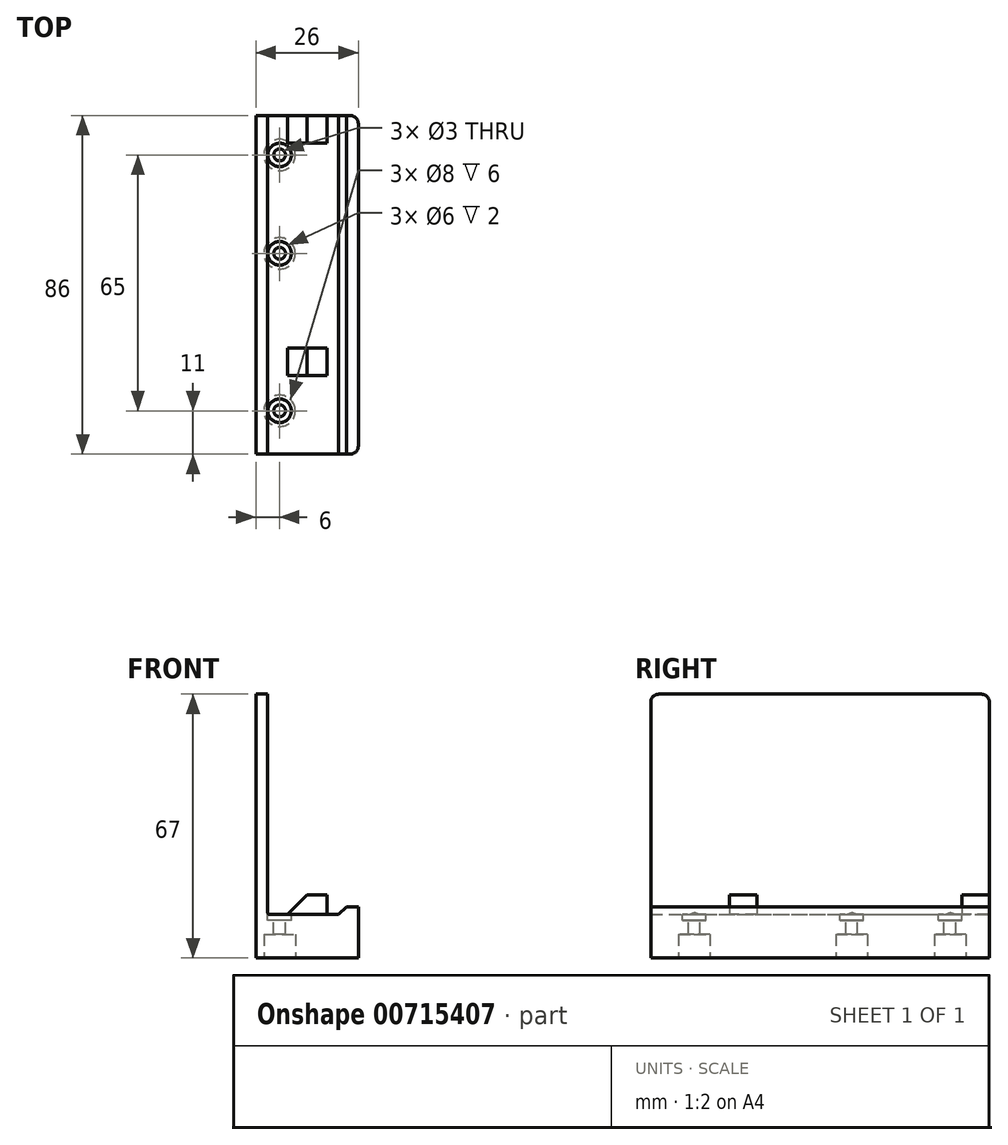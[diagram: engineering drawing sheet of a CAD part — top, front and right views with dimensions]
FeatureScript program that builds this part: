
annotation { "Feature Type Name" : "Feature", "Feature Type Description" : "" }
export const myFeature = defineFeature(function(context is Context, id is Id, definition is map)
    precondition{}
    {
        {
            var Q0;
            Q0=qCreatedBy(makeId("Front.planeOp"),FACE);
            var sketch = newSketch(context, id + "F0", { "sketchPlane" : qUnion([Q0])});
            skLineSegment(sketch, "E0", {"start": v(0, 67) * mm, "end": v(0, 11.5) * mm});
            skLineSegment(sketch, "E1", {"start": v(0, 67) * mm, "end": v(-3, 67) * mm});
            skLineSegment(sketch, "E2", {"start": v(-3, 67) * mm, "end": v(-3, 0) * mm});
            skLineSegment(sketch, "E3", {"start": v(-3, 0) * mm, "end": v(23, 0) * mm});
            skLineSegment(sketch, "E4", {"start": v(0.5, 11) * mm, "end": v(18, 11) * mm});
            skPoint(sketch, "E5.visualSharp", {"position": v(0, 11) * mm});
            skArc(sketch, "E5.filletArc", {"start": v(0, 11.5) * mm, "mid": v(0.15, 11.15) * mm, "end": v(0.5, 11) * mm});
            skLineSegment(sketch, "E6", {"start": v(20, 13) * mm, "end": v(23, 13) * mm});
            skLineSegment(sketch, "E7", {"start": v(23, 13) * mm, "end": v(23, 0) * mm});
            skLineSegment(sketch, "E8", {"start": v(18, 11) * mm, "end": v(20, 13) * mm});
            skSolve(sketch);
        }
        {
            var Q0;
            Q0=qSketchRegion(id+"F0",true);
            extrude(context, id + "F1", {"entities" : qUnion([Q0]), "endBound" : BoundingType.SYMMETRIC, "depth" : 86 * mm});
        }
        {
            var Q0;
            Q0=makeQuery(id+"F1.opExtrude","SWEPT_FACE",FACE,{"disambiguationData":[OSD([sQuery(id+"F0.wireOp",EDGE,"E3")])]});
            var sketch = newSketch(context, id + "F2", { "sketchPlane" : qUnion([Q0])});
            skCircle(sketch, "E9", {"center": v(3, -33) * mm, "radius": 4 * mm});
            skCircle(sketch, "E10", {"center": v(3, -8) * mm, "radius": 4 * mm});
            skCircle(sketch, "E11", {"center": v(3, 32) * mm, "radius": 4 * mm});
            skLineSegment(sketch, "E12", {"start": v(3, -46.09) * mm, "end": v(3, 49.3) * mm, "construction": true});
            skLineSegment(sketch, "E13", {"start": v(-6.86, -33) * mm, "end": v(12.39, -33) * mm, "construction": true});
            skLineSegment(sketch, "E14", {"start": v(-7.6, -8) * mm, "end": v(13.66, -8) * mm, "construction": true});
            skLineSegment(sketch, "E15", {"start": v(-7.39, 32) * mm, "end": v(13.66, 32) * mm, "construction": true});
            skSolve(sketch);
        }
        {
            var Q0;
            Q0=qSketchRegion(id+"F2",true);
            extrude(context, id + "F3", {"entities" : qUnion([Q0]), "operationType" : NewBodyOperationType.REMOVE, "oppositeDirection" : true, "depth" : 6 * mm});
        }
        {
            var Q0;
            Q0=makeQuery(id+"F1.opExtrude","SWEPT_FACE",FACE,{"disambiguationData":[OSD([sQuery(id+"F0.wireOp",EDGE,"E4")])]});
            var sketch = newSketch(context, id + "F4", { "sketchPlane" : qUnion([Q0])});
            skCircle(sketch, "E16", {"center": v(3, 33) * mm, "radius": 1.5 * mm});
            skCircle(sketch, "E17", {"center": v(3, 8) * mm, "radius": 1.5 * mm});
            skCircle(sketch, "E18", {"center": v(3, -32) * mm, "radius": 1.5 * mm});
            skCircle(sketch, "E19", {"center": v(3, 8) * mm, "radius": 3 * mm});
            skCircle(sketch, "E20", {"center": v(3, 33) * mm, "radius": 3 * mm});
            skCircle(sketch, "E21", {"center": v(3, -32) * mm, "radius": 3 * mm});
            skSolve(sketch);
        }
        {
            var Q0;
            Q0=makeQuery(id+"F4.imprint","IMPRINT",FACE,{"disambiguationData":[TD([[makeQuery(id+"F4.imprint","IMPRINT",EDGE,{"derivedFrom":sQuery(id+"F4.wireOp",EDGE,"E16")}),1.0]])]});
            var Q1;
            Q1=makeQuery(id+"F4.imprint","IMPRINT",FACE,{"disambiguationData":[TD([[makeQuery(id+"F4.imprint","IMPRINT",EDGE,{"derivedFrom":sQuery(id+"F4.wireOp",EDGE,"E17")}),1.0]])]});
            var Q2;
            Q2=makeQuery(id+"F4.imprint","IMPRINT",FACE,{"disambiguationData":[TD([[makeQuery(id+"F4.imprint","IMPRINT",EDGE,{"derivedFrom":sQuery(id+"F4.wireOp",EDGE,"E18")}),1.0]])]});
            extrude(context, id + "F5", {"entities" : qUnion([Q0, Q1, Q2]), "operationType" : NewBodyOperationType.REMOVE, "oppositeDirection" : true, "depth" : 25 * mm});
        }
        {
            var Q0;
            Q0=qSketchRegion(id+"F4",true);
            extrude(context, id + "F6", {"entities" : qUnion([Q0]), "operationType" : NewBodyOperationType.REMOVE, "endBound" : BoundingType.SYMMETRIC, "oppositeDirection" : true, "depth" : 3 * mm});
        }
        {
            var Q0;
            {var subQ1=sQuery(id+"F0.wireOp",EDGE,"E4");var subQ11=makeQuery(id+"F1.opExtrude","CAP_EDGE",EDGE,{"disambiguationData":[OSD([subQ1])],"isStart":true});Q0=makeQuery(id+"F4.imprint","IMPRINT",FACE,{"disambiguationData":[TD([[makeQuery(id+"F4.imprint","IMPRINT",EDGE,{"derivedFrom":subQ11}),-1.0]])]});}
            var sketch = newSketch(context, id + "F7", { "sketchPlane" : qUnion([Q0])});
            skLineSegment(sketch, "E22.bottom", {"start": v(5, 43) * mm, "end": v(15, 43) * mm});
            skLineSegment(sketch, "E22.top", {"start": v(5, 36) * mm, "end": v(15, 36) * mm});
            skLineSegment(sketch, "E22.left", {"start": v(5, 43) * mm, "end": v(5, 36) * mm});
            skLineSegment(sketch, "E22.right", {"start": v(15, 43) * mm, "end": v(15, 36) * mm});
            skLineSegment(sketch, "E23.bottom", {"start": v(5.02, -63.53) * mm, "end": v(22.73, -63.53) * mm, "construction": true});
            skLineSegment(sketch, "E23.top", {"start": v(5.02, -71.82) * mm, "end": v(22.73, -71.82) * mm, "construction": true});
            skLineSegment(sketch, "E23.left", {"start": v(5.02, -63.53) * mm, "end": v(5.02, -71.82) * mm, "construction": true});
            skLineSegment(sketch, "E23.right", {"start": v(22.73, -63.53) * mm, "end": v(22.73, -71.82) * mm, "construction": true});
            skLineSegment(sketch, "E24.bottom", {"start": v(5, -16) * mm, "end": v(15, -16) * mm});
            skLineSegment(sketch, "E24.top", {"start": v(5, -23) * mm, "end": v(15, -23) * mm});
            skLineSegment(sketch, "E24.left", {"start": v(5, -16) * mm, "end": v(5, -23) * mm});
            skLineSegment(sketch, "E24.right", {"start": v(15, -16) * mm, "end": v(15, -23) * mm});
            skSolve(sketch);
        }
        {
            var Q0;
            Q0=qSketchRegion(id+"F7",true);
            extrude(context, id + "F8", {"entities" : qUnion([Q0]), "operationType" : NewBodyOperationType.ADD, "depth" : 5 * mm});
        }
        {
            var Q0;
            Q0=qCreatedBy(makeId("Front.planeOp"),FACE);
            var sketch = newSketch(context, id + "F9", { "sketchPlane" : qUnion([Q0])});
            skLineSegment(sketch, "E25", {"start": v(5, 11) * mm, "end": v(13, 19) * mm});
            skLineSegment(sketch, "E26", {"start": v(13, 19) * mm, "end": v(5, 19) * mm});
            skLineSegment(sketch, "E27", {"start": v(5, 19) * mm, "end": v(5, 11) * mm});
            skSolve(sketch);
        }
        {
            var Q0;
            Q0=qSketchRegion(id+"F9",true);
            extrude(context, id + "F10", {"entities" : qUnion([Q0]), "operationType" : NewBodyOperationType.REMOVE, "endBound" : BoundingType.SYMMETRIC, "oppositeDirection" : true, "depth" : 100 * mm});
        }
        {
            var Q0;
            Q0=makeQuery(id+"F1.opExtrude","CAP_EDGE",EDGE,{"disambiguationData":[OSD([sQuery(id+"F0.wireOp",EDGE,"E7")])],"isStart":false});
            var Q1;
            Q1=makeQuery(id+"F1.opExtrude","CAP_EDGE",EDGE,{"disambiguationData":[OSD([sQuery(id+"F0.wireOp",EDGE,"E7")])],"isStart":true});
            var Q2;
            Q2=makeQuery(id+"F1.opExtrude","CAP_EDGE",EDGE,{"disambiguationData":[OSD([sQuery(id+"F0.wireOp",EDGE,"E1")])],"isStart":false});
            var Q3;
            Q3=makeQuery(id+"F1.opExtrude","CAP_EDGE",EDGE,{"disambiguationData":[OSD([sQuery(id+"F0.wireOp",EDGE,"E1")])],"isStart":true});
            fillet(context, id + "F11", {"entities" : qUnion([Q0, Q1, Q2, Q3]), "radius" : 2 * mm, "tangentPropagation" : true, "allowEdgeOverflow" : false});
        }
    });
